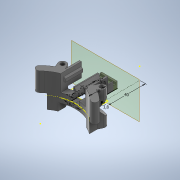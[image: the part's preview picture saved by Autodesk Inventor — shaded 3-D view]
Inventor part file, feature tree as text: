
AUTODESK INVENTOR PART (.ipt)
format: ipt  version: 2020 (Build 240168000, 168)  size: 671,232 bytes
history: native  units: mm
features: extrude x13, sketch x13, projected_geometry x10, other x3, sweep x1
ambient origin geometry x8: Origin, YZ Plane, XZ Plane, XY Plane, X Axis, Y Axis, Z Axis, Center Point
bodies: Body1 (feature_tree)
feature tree (40):
  other  "Твердое тело1"
  extrude  "Выдавливание1"  Depth=35.0mm TaperAngle=0.0deg
  sketch  "Эскиз2"
  extrude  "Выдавливание2"  Depth=4.0mm
  sweep  "Сдвиг1"
  extrude  "Выдавливание5"  Depth=8.0mm
  extrude  "Выдавливание6"  Depth=35.0mm TaperAngle=0.0deg
  extrude  "Выдавливание7"  Depth=8.5mm
  extrude  "Выдавливание8"  TaperAngle=45.0deg  [1 undecoded]
  other  "РабПлоскость1"
  extrude  "Выдавливание9"  Depth=8.5mm
  extrude  "Выдавливание10"  TaperAngle=45.0deg  [1 undecoded]
  extrude  "Выдавливание11"  TaperAngle=0.0deg  [1 undecoded]
  sketch  "Эскиз13"
  sketch  "Эскиз14"
  extrude  "Выдавливание12"  Depth=15.0mm TaperAngle=0.0deg
  extrude  "Выдавливание13"  Depth=5.0mm TaperAngle=0.0deg
  other  "РабПлоскость2"
  extrude  "Выдавливание14"  Depth=15.0mm TaperAngle=0.0deg
  extrude  "Выдавливание15"  Depth=26.0mm
  sketch  "Эскиз1"
  sketch  "Эскиз3"
  projected_geometry  "Спроецированная петля1"
  projected_geometry  "Спроецированная петля2"
  sketch  "3D эскиз1"
  sketch  "Эскиз4"
  sketch  "Эскиз6"
  projected_geometry  "Спроецированная петля4"
  sketch  "Эскиз7"
  projected_geometry  "Спроецированная петля5"
  sketch  "Эскиз9"
  projected_geometry  "Спроецированная петля7"
  sketch  "Эскиз11"
  projected_geometry  "Спроецированная петля8"
  sketch  "Эскиз12"
  projected_geometry  "Спроецированная петля9"
  projected_geometry  "Спроецированная петля10"
  sketch  "Эскиз16"
  projected_geometry  "Спроецированная петля15"
  projected_geometry  "Спроецированная петля16"
note: 3 required parameter values undecoded (feature->parameter linkage not recoverable at this tier; creation-order binding heuristic only, values carry confidence <= 0.55)
